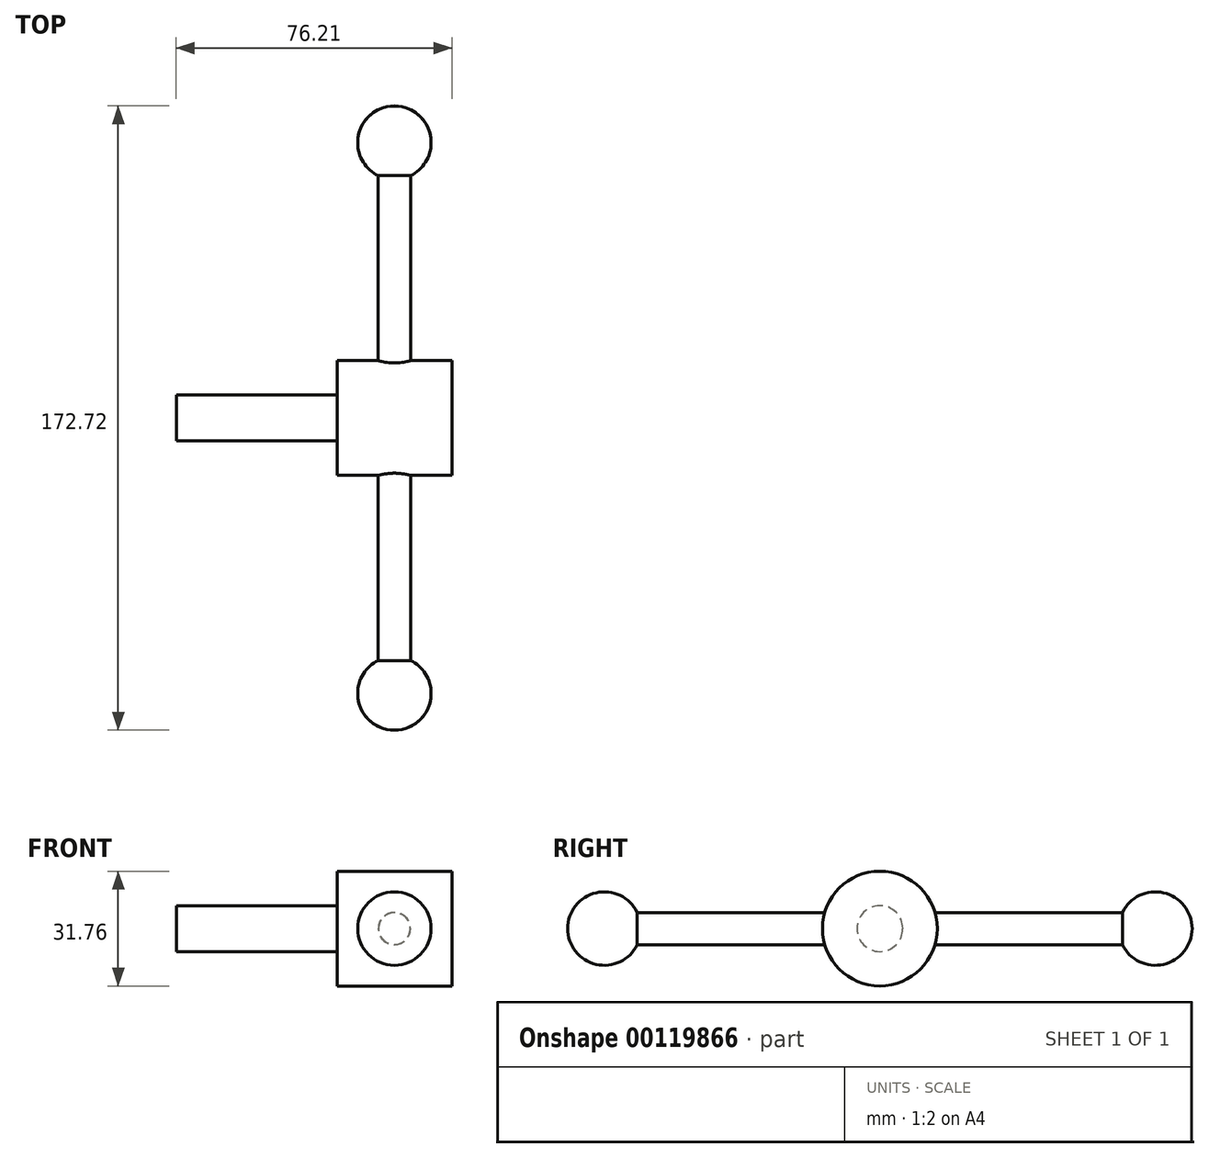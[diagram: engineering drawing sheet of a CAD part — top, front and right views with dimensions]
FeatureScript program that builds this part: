
annotation { "Feature Type Name" : "Feature", "Feature Type Description" : "" }
export const myFeature = defineFeature(function(context is Context, id is Id, definition is map)
    precondition{}
    {
        {
            var Q0;
            Q0=qCreatedBy(makeId("Right.planeOp"),FACE);
            var sketch = newSketch(context, id + "F0", { "sketchPlane" : qUnion([Q0])});
            skCircle(sketch, "E0", {"center": v(0, 0) * mm, "radius": 15.88 * mm});
            skSolve(sketch);
        }
        {
            var Q0;
            Q0 = qSketchRegion(id + "F0", true);
            extrude(context, id + "F1", {"entities" : qUnion([Q0]), "endBound" : BoundingType.SYMMETRIC, "depth" : 31.75 * mm});
        }
        {
            var Q0;
            Q0=makeQuery(id+"F1.opExtrude","CAP_FACE",FACE,{"disambiguationData":[OSD([sQuery(id+"F0.wireOp",EDGE,"E0")])],"isStart":true});
            var sketch = newSketch(context, id + "F2", { "sketchPlane" : qUnion([Q0])});
            skCircle(sketch, "E1", {"center": v(0, 0) * mm, "radius": 6.35 * mm});
            skSolve(sketch);
        }
        {
            var Q0;
            Q0 = qSketchRegion(id + "F2", true);
            extrude(context, id + "F3", {"entities" : qUnion([Q0]), "operationType" : NewBodyOperationType.ADD, "depth" : 44.45 * mm});
        }
        {
            var Q0;
            Q0=qCreatedBy(makeId("Front.planeOp"),FACE);
            var sketch = newSketch(context, id + "F4", { "sketchPlane" : qUnion([Q0])});
            skCircle(sketch, "E2", {"center": v(0, 0) * mm, "radius": 4.45 * mm});
            skSolve(sketch);
        }
        {
            var Q0;
            Q0 = qSketchRegion(id + "F4", true);
            extrude(context, id + "F5", {"entities" : qUnion([Q0]), "operationType" : NewBodyOperationType.ADD, "depth" : 76.2 * mm});
        }
        {
            var Q0;
            Q0=qCreatedBy(makeId("Front.planeOp"),FACE);
            var sketch = newSketch(context, id + "F6", { "sketchPlane" : qUnion([Q0])});
            skCircle(sketch, "E3", {"center": v(0, 0) * mm, "radius": 4.45 * mm});
            skSolve(sketch);
        }
        {
            var Q0;
            Q0 = qSketchRegion(id + "F6", true);
            extrude(context, id + "F7", {"entities" : qUnion([Q0]), "operationType" : NewBodyOperationType.ADD, "oppositeDirection" : true, "depth" : 76.2 * mm});
        }
        {
            var Q0;
            Q0=qCreatedBy(makeId("Top.planeOp"),FACE);
            var sketch = newSketch(context, id + "F8", { "sketchPlane" : qUnion([Q0])});
            skLineSegment(sketch, "E4.0", {"start": v(4.45, 76.2) * mm, "end": v(-4.45, 76.2) * mm});
            skLineSegment(sketch, "E5", {"start": v(-4.45, 15.88) * mm, "end": v(-4.45, 76.2) * mm});
            skLineSegment(sketch, "E6", {"start": v(4.45, 76.2) * mm, "end": v(4.45, 15.88) * mm});
            skArc(sketch, "E7", {"start": v(10.16, 76.2) * mm, "mid": v(0, 86.36) * mm, "end": v(-10.16, 76.2) * mm});
            skLineSegment(sketch, "E8", {"start": v(14.26, 76.2) * mm, "end": v(-22.93, 76.2) * mm, "construction": true});
            skLineSegment(sketch, "E9", {"start": v(10.16, 76.2) * mm, "end": v(-10.16, 76.2) * mm});
            skSolve(sketch);
        }
        {
            var Q0;
            {var subQ0=sQuery(id+"F8.wireOp",EDGE,"E7");Q0=makeQuery(id+"F8.imprint","IMPRINT",FACE,{"disambiguationData":[TD([[makeQuery(id+"F8.imprint","IMPRINT",EDGE,{"derivedFrom":subQ0}),1.0]])]});}
            var Q1;
            Q1=sQuery(id+"F8.wireOp",EDGE,"E8");
            revolve(context, id + "F9", {"operationType" : NewBodyOperationType.ADD, "entities" : qUnion([Q0]), "axis" : qUnion([Q1]), "revolveType" : RevolveType.FULL});
        }
        {
            var Q0;
            Q0=qCreatedBy(makeId("Top.planeOp"),FACE);
            var sketch = newSketch(context, id + "F10", { "sketchPlane" : qUnion([Q0])});
            skLineSegment(sketch, "E10.0", {"start": v(4.45, -76.2) * mm, "end": v(-4.45, -76.2) * mm});
            skLineSegment(sketch, "E11", {"start": v(-4.45, -76.2) * mm, "end": v(-4.45, -15.88) * mm});
            skLineSegment(sketch, "E12", {"start": v(4.45, -15.88) * mm, "end": v(4.45, -76.2) * mm});
            skLineSegment(sketch, "E13", {"start": v(0, -67.68) * mm, "end": v(0, -95.7) * mm, "construction": true});
            skPoint(sketch, "E13.endSnap0", {"position": v(0, -76.2) * mm});
            skLineSegment(sketch, "E14", {"start": v(-19.71, -76.2) * mm, "end": v(21.34, -76.2) * mm, "construction": true});
            skArc(sketch, "E15", {"start": v(-10.16, -76.2) * mm, "mid": v(0, -86.36) * mm, "end": v(10.16, -76.2) * mm});
            skLineSegment(sketch, "E16", {"start": v(-10.16, -76.2) * mm, "end": v(10.16, -76.2) * mm});
            skSolve(sketch);
        }
        {
            var Q0;
            {var subQ0=sQuery(id+"F10.wireOp",EDGE,"E15");Q0=makeQuery(id+"F10.imprint","IMPRINT",FACE,{"disambiguationData":[TD([[makeQuery(id+"F10.imprint","IMPRINT",EDGE,{"derivedFrom":subQ0}),1.0]])]});}
            var Q1;
            Q1=sQuery(id+"F10.wireOp",EDGE,"E14");
            revolve(context, id + "F11", {"operationType" : NewBodyOperationType.ADD, "entities" : qUnion([Q0]), "axis" : qUnion([Q1]), "revolveType" : RevolveType.FULL});
        }
    });
